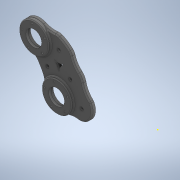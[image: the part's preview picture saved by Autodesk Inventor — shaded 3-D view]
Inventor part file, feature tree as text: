
AUTODESK INVENTOR PART (.ipt)
format: ipt  version: 2020 (Build 240168000, 168)  size: 348,672 bytes
history: native  units: mm
features: reference x8, sketch x5, other x4, extrude x4, chamfer x2
ambient origin geometry x8: Origin, YZ Plane, XZ Plane, XY Plane, X Axis, Y Axis, Z Axis, Center Point
bodies: Body1 (feature_tree)
feature tree (23):
  other  "Твердое тело1"
  other  "РабПлоскость1"
  extrude  "Выдавливание1"  Depth=47.8mm
  extrude  "Выдавливание2"  Depth=47.8mm
  chamfer  "Фаска1"  Distance=60.0mm
  chamfer  "Фаска2"  Distance=8.0mm
  sketch  "Эскиз3"
  extrude  "Выдавливание3"  Depth=8.0mm
  extrude  "Выдавливание4"  Depth=8.0mm
  sketch  "Эскиз1"
  reference  "Ссылка1"
  reference  "Ссылка2"
  reference  "Ссылка3"
  reference  "Ссылка4"
  reference  "Ссылка5"
  reference  "Ссылка6"
  sketch  "Эскиз2"
  reference  "Ссылка8"
  reference  "Ссылка9"
  sketch  "Эскиз4"
  sketch  "Эскиз5"
  other  "Сборка1"
  other  "block_new:1"
